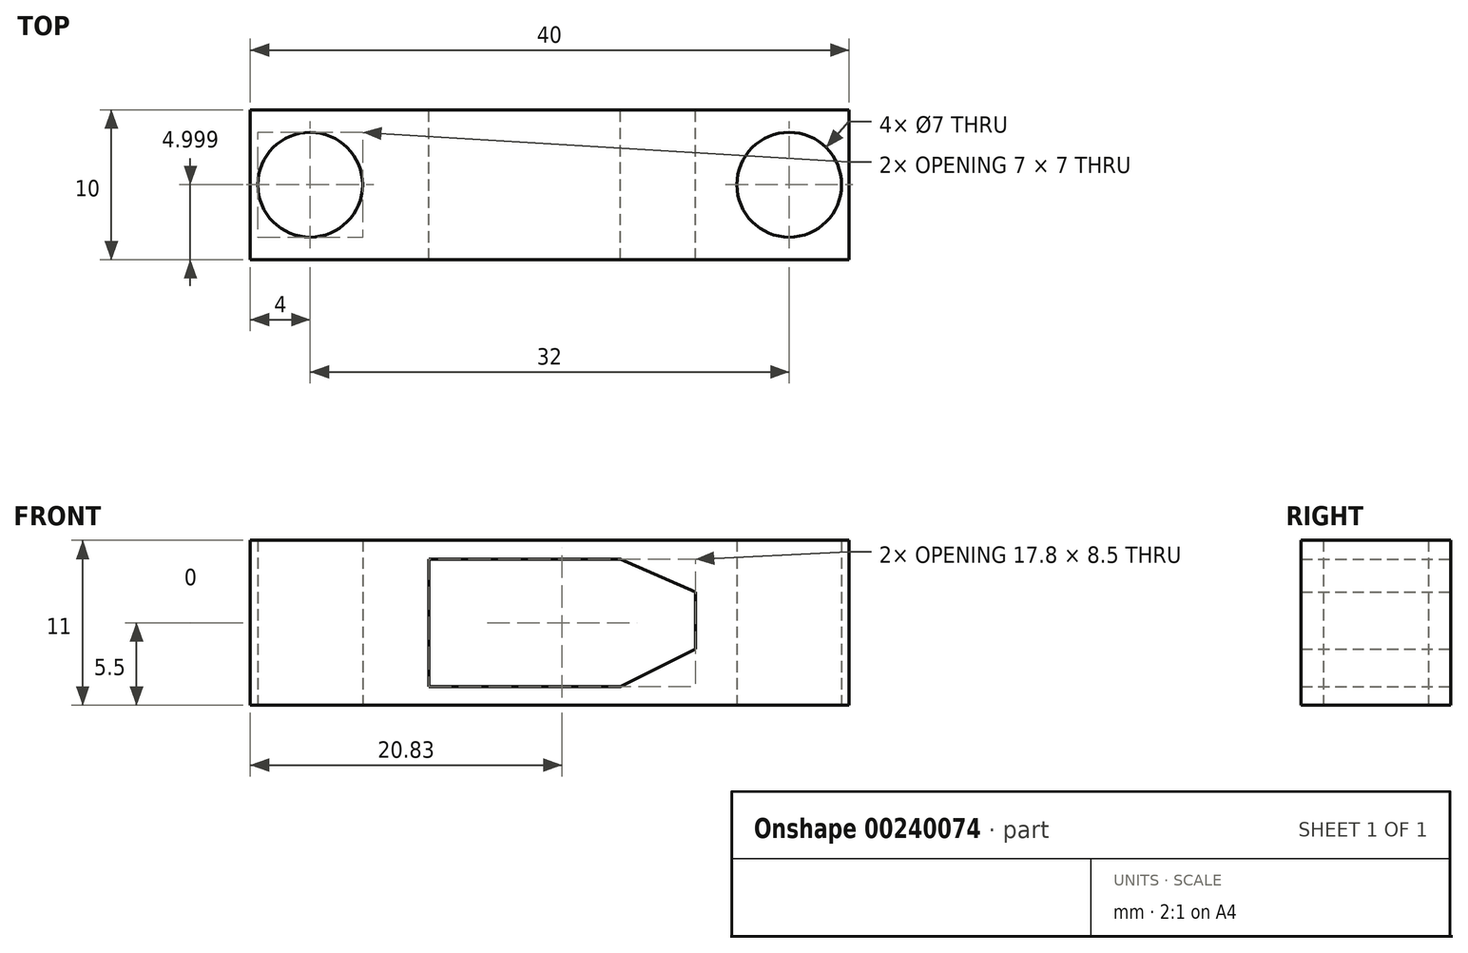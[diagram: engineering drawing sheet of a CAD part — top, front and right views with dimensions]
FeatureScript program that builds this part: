
annotation { "Feature Type Name" : "Feature", "Feature Type Description" : "" }
export const myFeature = defineFeature(function(context is Context, id is Id, definition is map)
    precondition{}
    {
        {
            var Q0;
            Q0=qCreatedBy(makeId("Top.planeOp"),FACE);
            var sketch = newSketch(context, id + "F0", { "sketchPlane" : qUnion([Q0])});
            skLineSegment(sketch, "E0.bottom", {"start": v(-24.73, 2.5) * mm, "end": v(15.27, 2.5) * mm});
            skLineSegment(sketch, "E0.top", {"start": v(-24.73, -7.5) * mm, "end": v(15.27, -7.5) * mm});
            skLineSegment(sketch, "E0.left", {"start": v(-24.73, 2.5) * mm, "end": v(-24.73, -7.5) * mm});
            skLineSegment(sketch, "E0.right", {"start": v(15.27, 2.5) * mm, "end": v(15.27, -7.5) * mm});
            skPoint(sketch, "E1", {"position": v(-20.73, -2.5) * mm});
            skPoint(sketch, "E2", {"position": v(11.27, -2.5) * mm});
            skSolve(sketch);
        }
        {
            var Q0;
            Q0=qSketchRegion(id+"F0",true);
            extrude(context, id + "F1", {"entities" : qUnion([Q0]), "depth" : 11 * mm});
        }
        {
            var Q0;
            Q0=sQuery(id+"F0.wireOp",VERTEX,"E1");
            var Q1;
            Q1=sQuery(id+"F0.wireOp",VERTEX,"E2");
            var Q2;
            Q2=makeQuery(id+"F1.opExtrude","SWEPT_BODY",BODY,{"disambiguationData":[OSD([sQuery(id+"F0.wireOp",EDGE,"E0.bottom"),sQuery(id+"F0.wireOp",EDGE,"E0.top"),sQuery(id+"F0.wireOp",EDGE,"E0.left"),sQuery(id+"F0.wireOp",EDGE,"E0.right")])]});
            hole(context, id + "F2", {"style" : HoleStyle.SIMPLE, "endStyle" : HoleEndStyle.THROUGH, "oppositeDirection" : true, "holeDiameter" : 7 * mm, "locations" : qUnion([Q0, Q1]), "scope" : qUnion([Q2]), "isTappedThrough" : true});
        }
        {
            var Q0;
            Q0=qCreatedBy(makeId("Front.planeOp"),FACE);
            var sketch = newSketch(context, id + "F3", { "sketchPlane" : qUnion([Q0])});
            skLineSegment(sketch, "E3.left", {"start": v(-12.8, 9.75) * mm, "end": v(-12.8, 1.25) * mm});
            skPoint(sketch, "E4", {"position": v(0, 9.75) * mm});
            skPoint(sketch, "E5", {"position": v(0, 1.25) * mm});
            skPoint(sketch, "E6", {"position": v(5, 7.55) * mm});
            skPoint(sketch, "E7", {"position": v(5, 3.75) * mm});
            skLineSegment(sketch, "E8", {"start": v(0, 9.75) * mm, "end": v(5, 7.55) * mm});
            skLineSegment(sketch, "E9", {"start": v(5, 3.75) * mm, "end": v(0, 1.25) * mm});
            skLineSegment(sketch, "E10", {"start": v(-12.8, 9.75) * mm, "end": v(0, 9.75) * mm});
            skLineSegment(sketch, "E11", {"start": v(5, 7.55) * mm, "end": v(5, 3.75) * mm});
            skLineSegment(sketch, "E12", {"start": v(0, 1.25) * mm, "end": v(-12.8, 1.25) * mm});
            skSolve(sketch);
        }
        {
            var Q0;
            Q0=qSketchRegion(id+"F3",true);
            extrude(context, id + "F4", {"entities" : qUnion([Q0]), "operationType" : NewBodyOperationType.REMOVE, "endBound" : BoundingType.SYMMETRIC, "depth" : 22 * mm});
        }
        {
            var Q0;
            Q0=makeQuery(id+"F1.opExtrude","SWEPT_BODY",BODY,{"disambiguationData":[OSD([sQuery(id+"F0.wireOp",EDGE,"E0.bottom"),sQuery(id+"F0.wireOp",EDGE,"E0.top"),sQuery(id+"F0.wireOp",EDGE,"E0.left"),sQuery(id+"F0.wireOp",EDGE,"E0.right")])]});
            transform(context, id + "F5", {"entities" : qUnion([Q0]), "transformType" : TransformType.TRANSLATION_3D, "dx" : 0 * mm, "dy" : 0 * mm, "dz" : 0 * mm, "makeCopy" : true});
        }
    });
